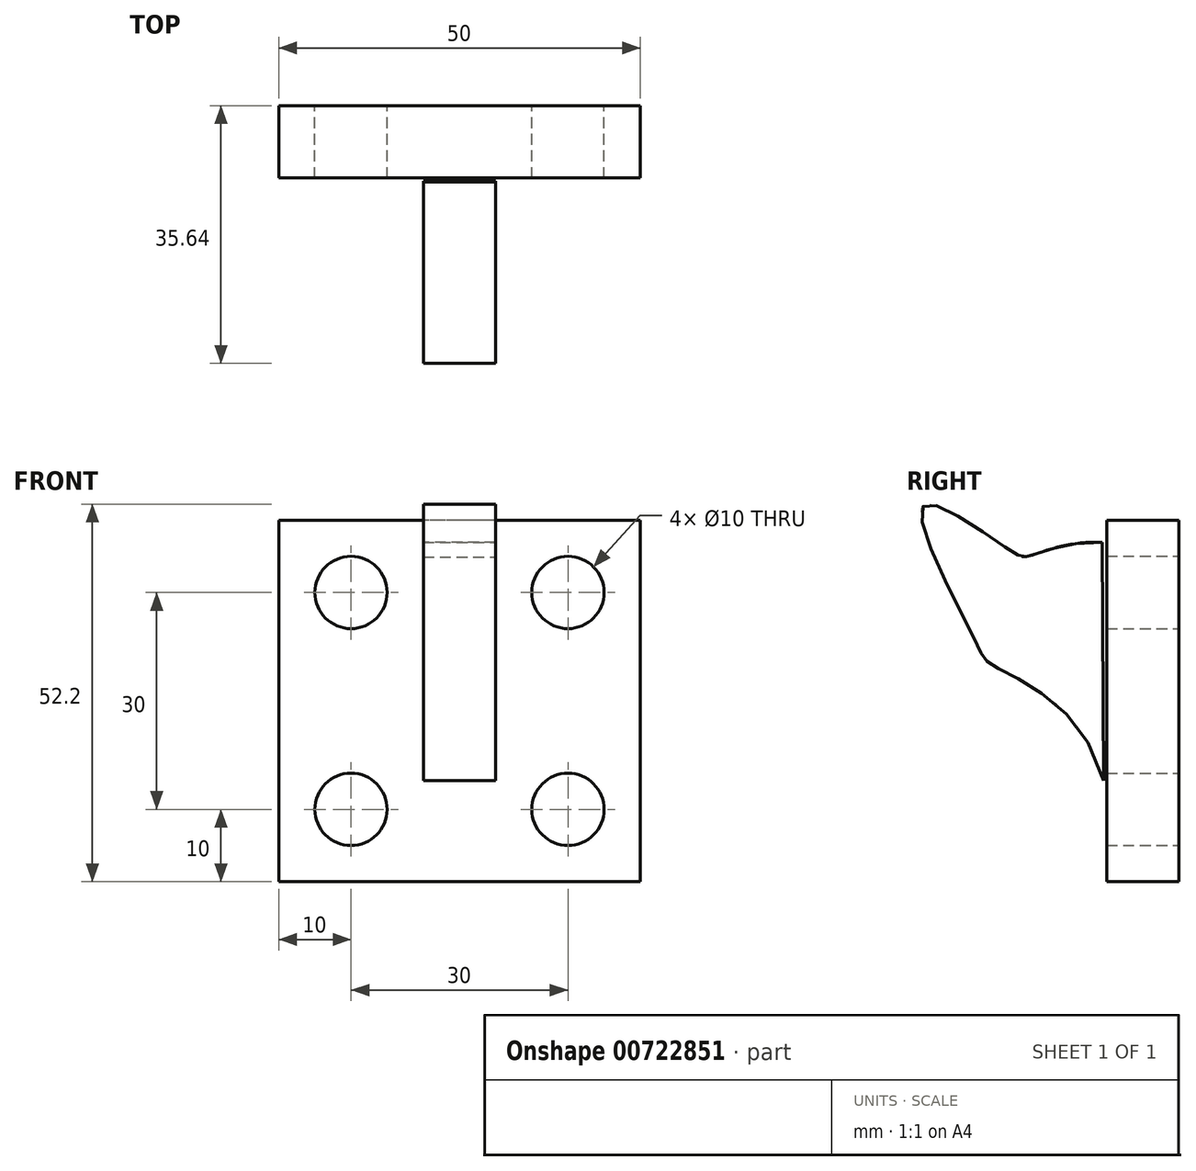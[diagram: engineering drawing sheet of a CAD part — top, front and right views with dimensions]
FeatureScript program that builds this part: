
annotation { "Feature Type Name" : "Feature", "Feature Type Description" : "" }
export const myFeature = defineFeature(function(context is Context, id is Id, definition is map)
    precondition{}
    {
        {
            var Q0;
            Q0=qCreatedBy(makeId("Front.planeOp"),FACE);
            var sketch = newSketch(context, id + "F0", { "sketchPlane" : qUnion([Q0])});
            skLineSegment(sketch, "E0.bottom", {"start": v(25, 25) * mm, "end": v(-25, 25) * mm});
            skLineSegment(sketch, "E0.top", {"start": v(25, -25) * mm, "end": v(-25, -25) * mm});
            skLineSegment(sketch, "E0.left", {"start": v(25, 25) * mm, "end": v(25, -25) * mm});
            skLineSegment(sketch, "E0.right", {"start": v(-25, 25) * mm, "end": v(-25, -25) * mm});
            skPoint(sketch, "E0.middle", {"position": v(0, 0) * mm});
            skLineSegment(sketch, "E1.bottom", {"start": v(-25, 25) * mm, "end": v(-15, 25) * mm});
            skLineSegment(sketch, "E1.top", {"start": v(-25, 15) * mm, "end": v(-15, 15) * mm});
            skLineSegment(sketch, "E1.left", {"start": v(-25, 25) * mm, "end": v(-25, 15) * mm});
            skLineSegment(sketch, "E1.right", {"start": v(-15, 25) * mm, "end": v(-15, 15) * mm});
            skCircle(sketch, "E2", {"center": v(-15, 15) * mm, "radius": 5 * mm});
            skLineSegment(sketch, "E3", {"start": v(0, 0) * mm, "end": v(0, 9.11) * mm});
            skLineSegment(sketch, "E4", {"start": v(0, 0) * mm, "end": v(-11.5, 0) * mm});
            skCircle(sketch, "E5.MirrorC", {"center": v(15, 15) * mm, "radius": 5 * mm});
            skCircle(sketch, "E6.MirrorC", {"center": v(-15, -15) * mm, "radius": 5 * mm});
            skCircle(sketch, "E7.MirrorC", {"center": v(15, -15) * mm, "radius": 5 * mm});
            skPoint(sketch, "E8.endSnap0", {"position": v(-25, 0) * mm});
            skSolve(sketch);
        }
        {
            var Q0;
            {var subQ1=sQuery(id+"F0.wireOp",EDGE,"E0.bottom");Q0=makeQuery(id+"F0.imprint","IMPRINT",FACE,{"disambiguationData":[TD([[makeQuery(id+"F0.imprint","IMPRINT",EDGE,{"derivedFrom":subQ1}),1.0]])]});}
            var Q1;
            {var subQ1=sQuery(id+"F0.wireOp",EDGE,"E1.bottom");Q1=makeQuery(id+"F0.imprint","IMPRINT",FACE,{"disambiguationData":[TD([[makeQuery(id+"F0.imprint","IMPRINT",EDGE,{"derivedFrom":subQ1}),-1.0]])]});}
            extrude(context, id + "F1", {"entities" : qUnion([Q0, Q1]), "depth" : 10 * mm, "offsetDistance" : 25 * mm});
        }
        {
            var Q0;
            Q0=makeQuery(id+"F1.opExtrude","SWEPT_EDGE",EDGE,{"disambiguationData":[OSD([sQuery(id+"F0.wireOp",EDGE,"E0.top"),sQuery(id+"F0.wireOp",EDGE,"E0.right")])]});
            var Q1;
            Q1=makeQuery(id+"F1.opExtrude","SWEPT_EDGE",EDGE,{"disambiguationData":[OSD([sQuery(id+"F0.wireOp",EDGE,"E0.top"),sQuery(id+"F0.wireOp",EDGE,"E0.left")])]});
            var Q2;
            Q2=makeQuery(id+"F1.opExtrude","SWEPT_EDGE",EDGE,{"disambiguationData":[OSD([sQuery(id+"F0.wireOp",EDGE,"E0.bottom"),sQuery(id+"F0.wireOp",EDGE,"E0.left")])]});
            var Q3;
            Q3=makeQuery(id+"F1.opExtrude","SWEPT_EDGE",EDGE,{"disambiguationData":[OSD([sQuery(id+"F0.wireOp",EDGE,"E1.bottom"),sQuery(id+"F0.wireOp",EDGE,"E1.left")])]});
            fillet(context, id + "F2", {"entities" : qUnion([Q0, Q1, Q2, Q3]), "radius" : 3.14 * mm, "tangentPropagation" : true, "allowEdgeOverflow" : false});
        }
        {
            var Q0;
            Q0 = qSketchRegion(id + "F0", true);
            extrude(context, id + "F3", {"entities" : qUnion([Q0]), "operationType" : NewBodyOperationType.ADD, "depth" : 10 * mm, "offsetDistance" : 25 * mm});
        }
        {
            var Q0;
            Q0=qCreatedBy(makeId("Right.planeOp"),FACE);
            var sketch = newSketch(context, id + "F4", { "sketchPlane" : qUnion([Q0])});
            skFitSpline(sketch, "E9", {"points": [v(-10.42, -11.02) * mm, v(-25.93, 5.02) * mm, v(-28.2, 8.39) * mm, v(-35.3, 26.98) * mm, v(-23.23, 20.75) * mm, v(-20.77, 20.03) * mm, v(-10.58, 21.95) * mm], "startDerivative": vector(-35.6, 137.9) * mm, "endDerivative": vector(92.65, -3.53) * mm});
            skLineSegment(sketch, "E10", {"start": v(-10.58, 21.95) * mm, "end": v(-10.42, -11.02) * mm});
            skSolve(sketch);
        }
        {
            var Q0;
            Q0=makeQuery(id+"F4.imprint","IMPRINT",FACE,{"disambiguationData":[TD([[makeQuery(id+"F4.imprint","IMPRINT",EDGE,{"derivedFrom":sQuery(id+"F4.wireOp",EDGE,"E9")}),-1.0]])]});
            extrude(context, id + "F5", {"entities" : qUnion([Q0]), "depth" : 5 * mm, "offsetDistance" : 25 * mm, "hasSecondDirection" : true, "secondDirectionOppositeDirection" : true, "secondDirectionDepth" : 5 * mm});
        }
    });
